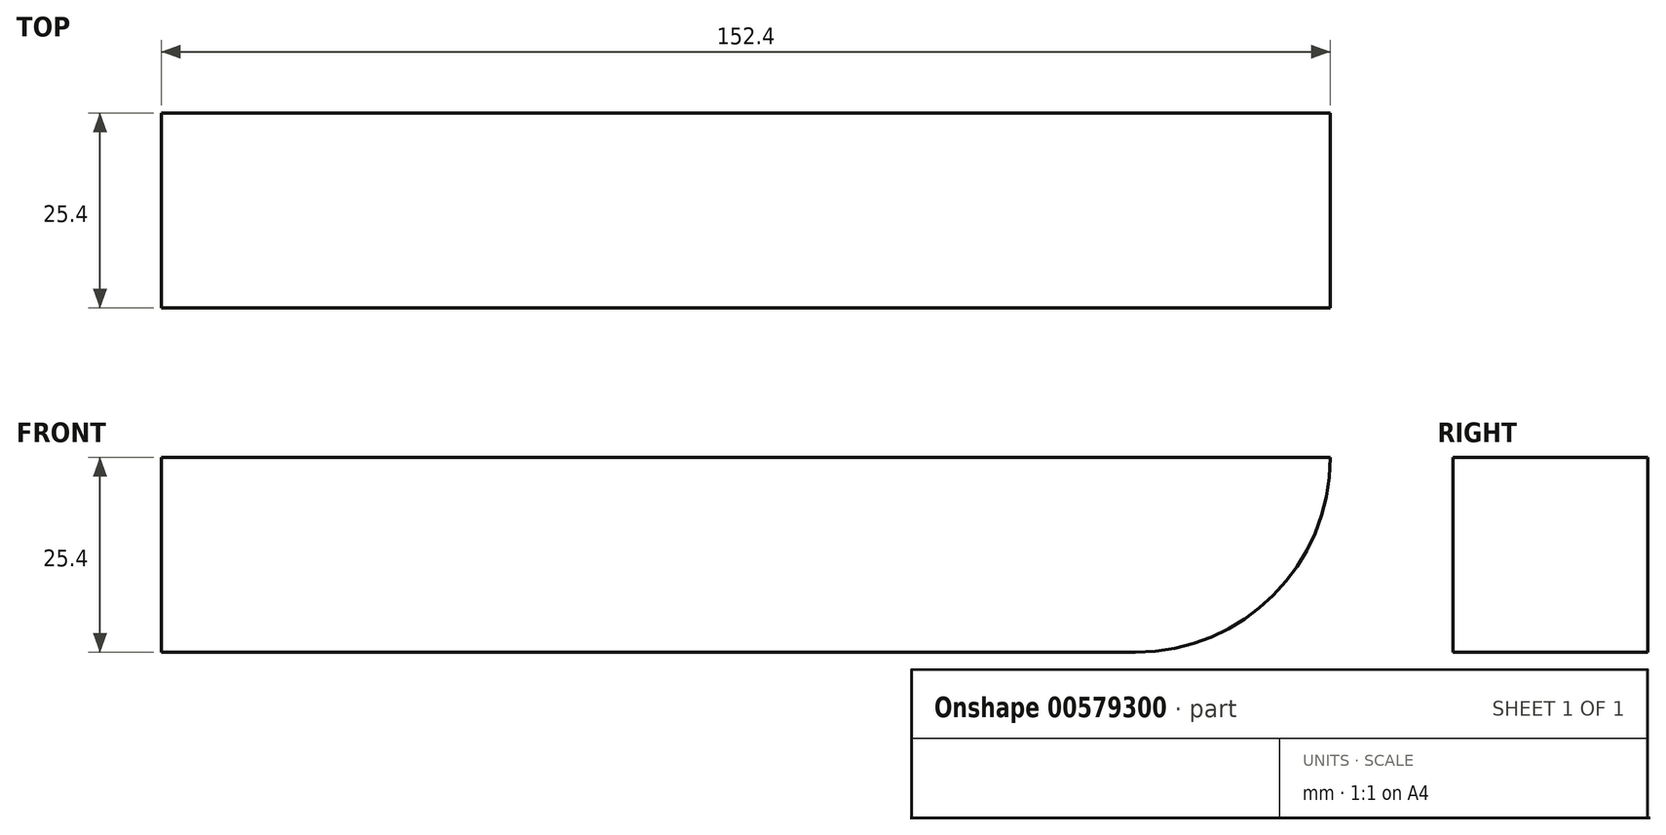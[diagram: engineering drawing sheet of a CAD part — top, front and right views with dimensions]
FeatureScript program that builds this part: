
annotation { "Feature Type Name" : "Feature", "Feature Type Description" : "" }
export const myFeature = defineFeature(function(context is Context, id is Id, definition is map)
    precondition{}
    {
        {
            var Q0;
            Q0=qCreatedBy(makeId("Front.planeOp"),FACE);
            var sketch = newSketch(context, id + "F0", { "sketchPlane" : qUnion([Q0])});
            skLineSegment(sketch, "E0.bottom", {"start": v(-63.35, -8.34) * mm, "end": v(63.65, -8.34) * mm});
            skLineSegment(sketch, "E0.top", {"start": v(-63.35, -33.74) * mm, "end": v(63.65, -33.74) * mm});
            skLineSegment(sketch, "E0.left", {"start": v(-63.35, -8.34) * mm, "end": v(-63.35, -33.74) * mm});
            skLineSegment(sketch, "E0.right", {"start": v(63.65, -8.34) * mm, "end": v(63.65, -33.74) * mm});
            skLineSegment(sketch, "E1", {"start": v(63.65, -11.53) * mm, "end": v(63.65, -33.74) * mm});
            skLineSegment(sketch, "E2", {"start": v(63.65, -8.34) * mm, "end": v(89.05, -8.34) * mm});
            skArc(sketch, "E3", {"start": v(63.65, -33.74) * mm, "mid": v(81.6, -26.3) * mm, "end": v(89.05, -8.34) * mm});
            skSolve(sketch);
        }
        {
            var Q0;
            Q0=makeQuery(id+"F0.imprint","IMPRINT",FACE,{"disambiguationData":[TD([[makeQuery(id+"F0.imprint","IMPRINT",EDGE,{"derivedFrom":sQuery(id+"F0.wireOp",EDGE,"E0.right")}),1.0]])]});
            var Q1;
            Q1=makeQuery(id+"F0.imprint","IMPRINT",FACE,{"disambiguationData":[TD([[makeQuery(id+"F0.imprint","IMPRINT",EDGE,{"derivedFrom":sQuery(id+"F0.wireOp",EDGE,"E0.bottom")}),-1.0]])]});
            extrude(context, id + "F1", {"entities" : qUnion([Q0, Q1]), "depth" : 25.4 * mm, "offsetDistance" : 25.4 * mm});
        }
    });
